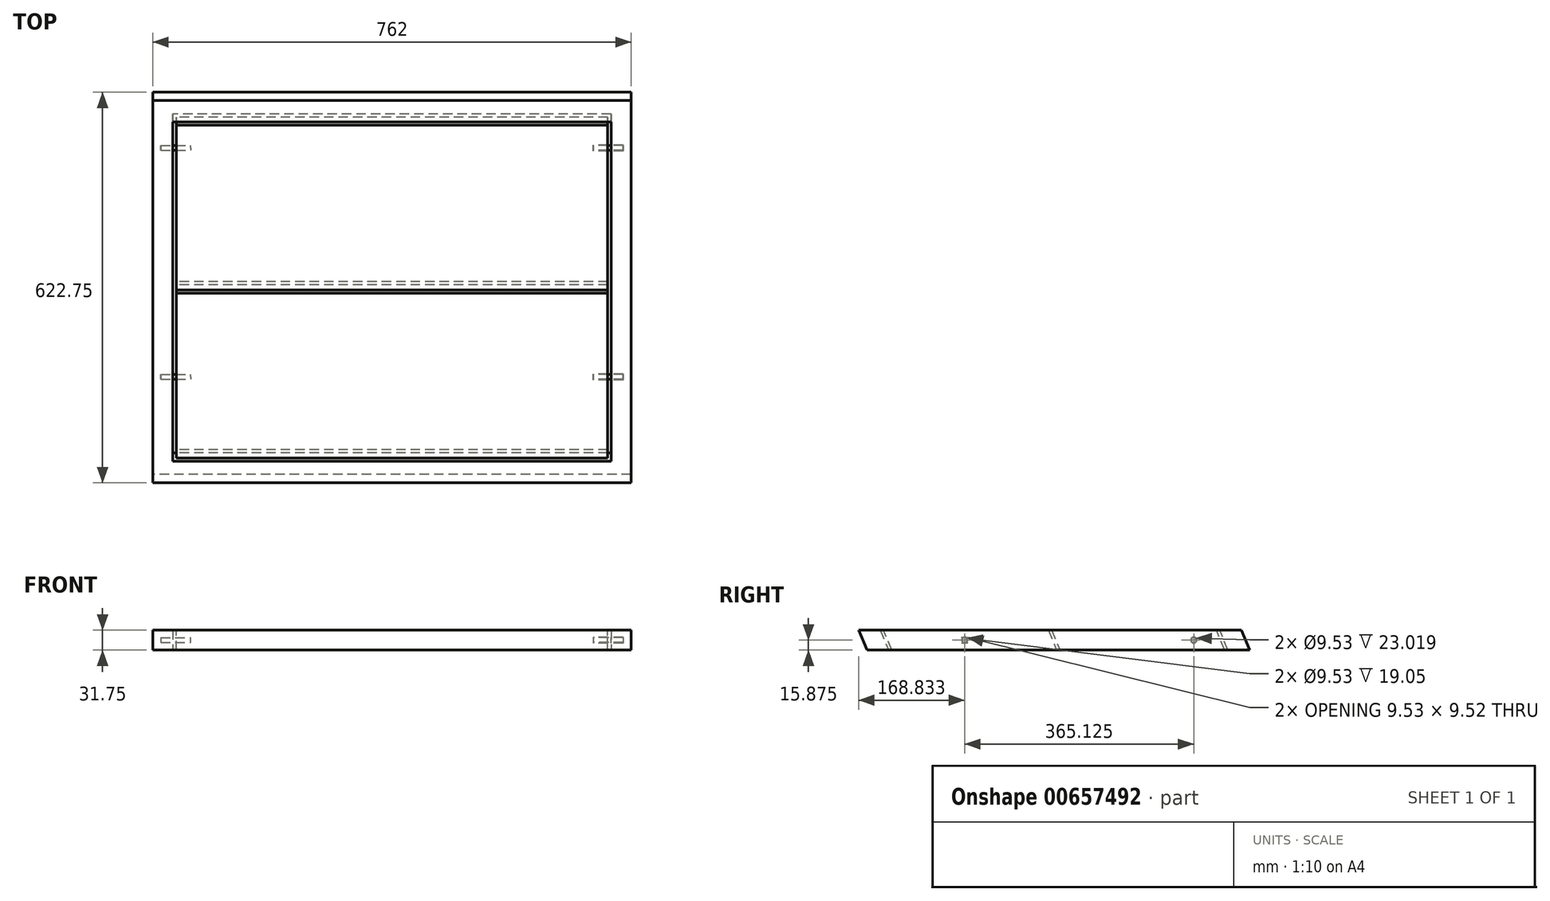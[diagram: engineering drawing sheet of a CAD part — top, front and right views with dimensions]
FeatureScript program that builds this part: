
annotation { "Feature Type Name" : "Feature", "Feature Type Description" : "" }
export const myFeature = defineFeature(function(context is Context, id is Id, definition is map)
    precondition{}
    {
        {
            var Q0;
            Q0=qCreatedBy(makeId("Right.planeOp"),FACE);
            var sketch = newSketch(context, id + "F0", { "sketchPlane" : qUnion([Q0])});
            skLineSegment(sketch, "E0", {"start": v(-304.8, 0) * mm, "end": v(304.8, 0) * mm});
            skLineSegment(sketch, "E1", {"start": v(304.8, 0) * mm, "end": v(291.65, 31.75) * mm});
            skLineSegment(sketch, "E2", {"start": v(291.65, 31.75) * mm, "end": v(-317.95, 31.75) * mm});
            skLineSegment(sketch, "E3", {"start": v(-317.95, 31.75) * mm, "end": v(-304.8, 0) * mm});
            skSolve(sketch);
        }
        {
            var Q0;
            Q0 = qSketchRegion(id + "F0", true);
            extrude(context, id + "F1", {"entities" : qUnion([Q0]), "endBound" : BoundingType.SYMMETRIC, "depth" : 762 * mm, "offsetDistance" : 25.4 * mm});
        }
        {
            var Q0;
            Q0=makeQuery(id+"F1.opExtrude","SWEPT_FACE",FACE,{"disambiguationData":[OSD([sQuery(id+"F0.wireOp",EDGE,"E2")])]});
            var Q1;
            Q1=makeQuery(id+"F1.opExtrude","SWEPT_FACE",FACE,{"disambiguationData":[OSD([sQuery(id+"F0.wireOp",EDGE,"E0")])]});
            shell(context, id + "F2", {"entities" : qUnion([Q0, Q1]), "thickness" : 31.75 * mm});
        }
        {
            var Q0;
            Q0=qCreatedBy(makeId("Right.planeOp"),FACE);
            var sketch = newSketch(context, id + "F3", { "sketchPlane" : qUnion([Q0])});
            skLineSegment(sketch, "E4", {"start": v(-278.43, 31.75) * mm, "end": v(-15.73, 31.75) * mm});
            skLineSegment(sketch, "E5", {"start": v(-15.73, 31.75) * mm, "end": v(-2.58, 0) * mm});
            skLineSegment(sketch, "E6", {"start": v(-2.58, 0) * mm, "end": v(-265.28, 0) * mm});
            skLineSegment(sketch, "E7", {"start": v(-265.28, 0) * mm, "end": v(-278.43, 31.75) * mm});
            skLineSegment(sketch, "E8", {"start": v(252.13, 31.75) * mm, "end": v(-10.57, 31.75) * mm});
            skLineSegment(sketch, "E9", {"start": v(-10.57, 31.75) * mm, "end": v(2.58, 0) * mm});
            skLineSegment(sketch, "E10", {"start": v(2.58, 0) * mm, "end": v(265.28, 0) * mm});
            skLineSegment(sketch, "E11", {"start": v(265.28, 0) * mm, "end": v(252.13, 31.75) * mm});
            skSolve(sketch);
        }
        {
            var Q0;
            Q0 = qSketchRegion(id + "F3", true);
            extrude(context, id + "F4", {"entities" : qUnion([Q0]), "endBound" : BoundingType.SYMMETRIC, "depth" : 687.4 * mm, "offsetDistance" : 25.4 * mm});
        }
        {
            var Q0;
            {var subQ0=sQuery(id+"F0.wireOp",EDGE,"E3");var subQ1=sQuery(id+"F0.wireOp",EDGE,"E2");var subQ2=sQuery(id+"F0.wireOp",EDGE,"E1");var subQ3=sQuery(id+"F0.wireOp",EDGE,"E0");Q0=makeQuery(id+"F2.opShell","OFFSET_FACE",FACE,{"disambiguationData":[OSD([subQ3,subQ2,subQ1,subQ0]),TDD([makeQuery(id+"F1.opExtrude","CAP_FACE",FACE,{"disambiguationData":[OSD([subQ3,subQ2,subQ1,subQ0])],"isStart":false})])]});}
            var sketch = newSketch(context, id + "F5", { "sketchPlane" : qUnion([Q0])});
            skCircle(sketch, "E12", {"center": v(-216, 15.88) * mm, "radius": 4.76 * mm});
            skLineSegment(sketch, "E13", {"start": v(-216, 0) * mm, "end": v(-216, 31.75) * mm, "construction": true});
            skLineSegment(sketch, "E14.1.0.0", {"start": v(149.12, 0) * mm, "end": v(149.12, 31.75) * mm, "construction": true});
            skCircle(sketch, "E14.1.0.1", {"center": v(149.12, 15.88) * mm, "radius": 4.76 * mm});
            skLineSegment(sketch, "E14.direction1", {"start": v(-216, 0) * mm, "end": v(149.12, 0) * mm, "construction": true});
            skSolve(sketch);
        }
        {
            var Q0;
            Q0 = qSketchRegion(id + "F5", true);
            extrude(context, id + "F6", {"entities" : qUnion([Q0]), "operationType" : NewBodyOperationType.REMOVE, "oppositeDirection" : true, "depth" : 19.05 * mm, "offsetDistance" : 25.4 * mm, "hasSecondDirection" : true, "secondDirectionOppositeDirection" : false, "secondDirectionDepth" : 28.57 * mm});
        }
        {
            var Q0;
            Q0=makeQuery(id+"F6.boolean.opBoolean","COPY",FACE,{"derivedFrom":makeQuery(id+"F6.opExtrude","CAP_FACE",FACE,{"disambiguationData":[OSD([sQuery(id+"F5.wireOp",EDGE,"E12")])],"isStart":true})});
            var sketch = newSketch(context, id + "F7", { "sketchPlane" : qUnion([Q0])});
            skCircle(sketch, "E15", {"center": v(216, 15.88) * mm, "radius": 3.97 * mm});
            skCircle(sketch, "E16", {"center": v(-149.12, 15.88) * mm, "radius": 3.97 * mm});
            skSolve(sketch);
        }
        {
            var Q0;
            Q0 = qSketchRegion(id + "F7", true);
            var Q1;
            Q1=makeQuery(id+"F6.boolean.opBoolean","COPY",FACE,{"derivedFrom":makeQuery(id+"F6.opExtrude","CAP_FACE",FACE,{"disambiguationData":[OSD([sQuery(id+"F5.wireOp",EDGE,"E12")])],"isStart":false})});
            extrude(context, id + "F8", {"entities" : qUnion([Q0]), "endBound" : BoundingType.UP_TO_SURFACE, "depth" : 25.4 * mm, "endBoundEntityFace" : qUnion([Q1]), "offsetDistance" : 25.4 * mm});
        }
        {
            var Q0;
            Q0=makeQuery(id+"F8.opExtrude","SWEPT_BODY",BODY,{"disambiguationData":[OSD([sQuery(id+"F7.wireOp",EDGE,"E15")])]});
            var Q1;
            Q1=makeQuery(id+"F8.opExtrude","SWEPT_BODY",BODY,{"disambiguationData":[OSD([sQuery(id+"F7.wireOp",EDGE,"E16")])]});
            var Q2;
            Q2=qCreatedBy(makeId("Right.planeOp"),FACE);
            mirror(context, id + "F9", {"entities" : qUnion([Q0, Q1]), "mirrorPlane" : qUnion([Q2])});
        }
    });
